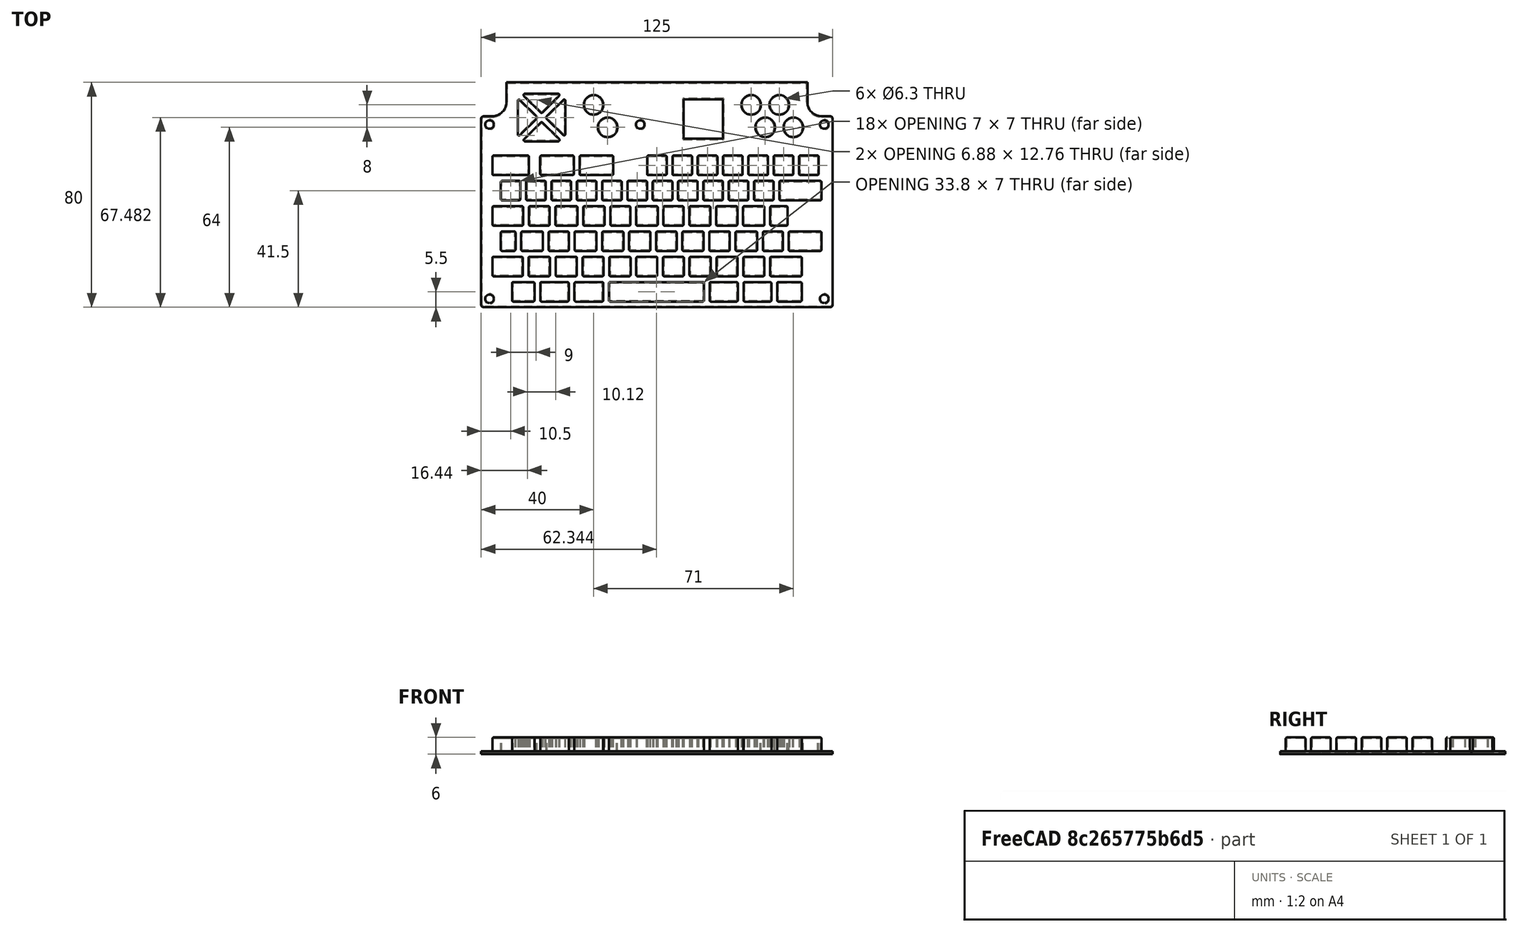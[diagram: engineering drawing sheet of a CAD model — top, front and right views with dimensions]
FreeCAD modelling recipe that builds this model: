
FCSTD DOCUMENT  (FreeCAD 0.20R29603 (Git))
Label: keypad
License: All rights reserved
LicenseURL: http://en.wikipedia.org/wiki/All_rights_reserved
objects: Image::ImagePlane×1, Part::Feature×1, PartDesign::FeatureBase×1, PartDesign::Thickness×1, PartDesign::Body×1
note: 5 computed .brp shape members not serialized (recipe doc carries the construction recipe); baked Part::Feature solids carry a one-line shape summary decoded from their .brp

FEATURE [Image::ImagePlane] ImagePlane
  Placement = pos=(0,4,3) rot=(0,0,1;0rad)
  XSize = 127.993
  YSize = 91.091
FEATURE [Part::Feature] Pocket007001001  label="keypad"
  shape: bbox 125 x 80 x 6.002 mm, 1166 faces (baked)
FEATURE [PartDesign::FeatureBase] BaseFeature
  BaseFeature = -> Pocket007001001
FEATURE [PartDesign::Thickness] Thickness
  Base = -> BaseFeature [Face15]
  BaseFeature = -> BaseFeature
  Intersection = false
  Join = 0
  Mode = 0
  Reversed = true
  SupportTransform = false
  Value = 0.35
FEATURE [PartDesign::Body] Body
  BaseFeature = -> Pocket007001001
  Group = -> [BaseFeature,Thickness]
  Origin = -> Origin
  Tip = -> Thickness
